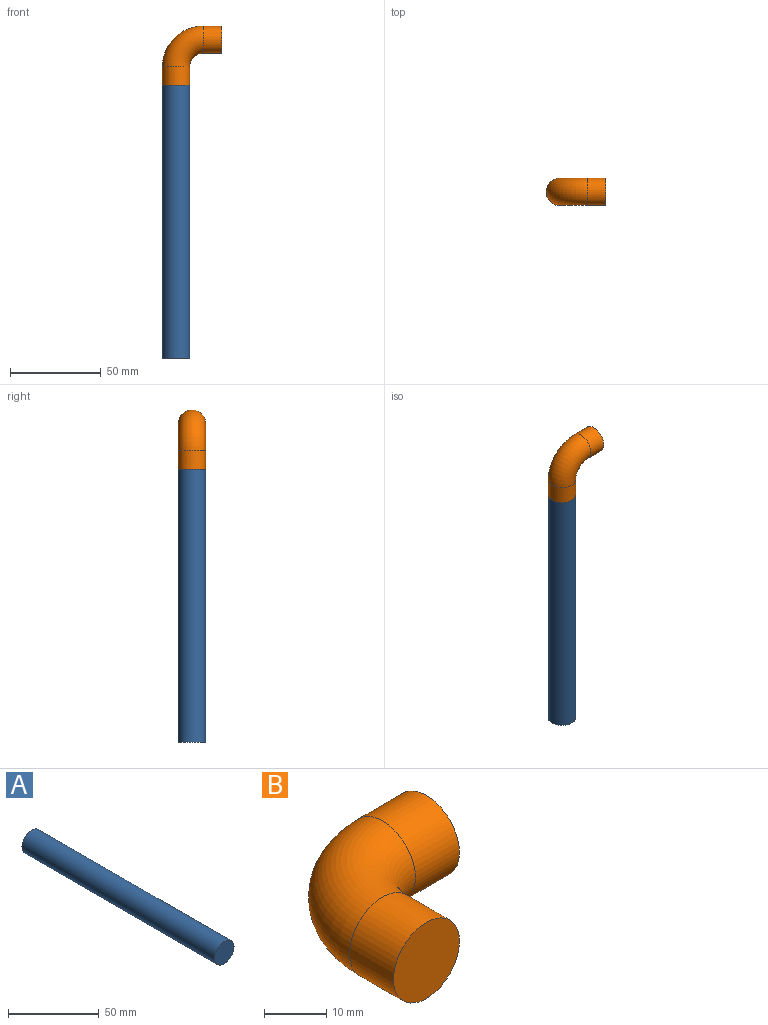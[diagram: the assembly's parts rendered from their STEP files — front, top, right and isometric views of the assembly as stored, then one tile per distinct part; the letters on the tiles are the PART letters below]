
ASSEMBLY  parts=2 mates=1
PART A: 3 faces, bbox 15x150x15 mm
  f0: cylinder r=7.5mm len=150mm, axis (0,1,0), area 7068.6mm2, adj f1,f2
  f1: plane 15x15mm, normal (0,-1,0), area 176.7mm2, adj f0
  f2: plane 15x15mm, normal (0,1,0), area 176.7mm2, adj f0
PART B: 5 faces, bbox 34.4x34.4x15 mm
  f0: plane 15x15mm, normal (0,-1,0), area 176.7mm2, adj f2
  f1: plane 15x15mm, normal (1,0,0), area 176.7mm2, adj f4
  f2: cylinder r=7.5mm len=15mm, axis (0,1,0), area 471.2mm2, adj f0,f3
  f3: torus R=15mm, axis (0,0,-1), area 1110.3mm2, adj f2,f4
  f4: cylinder r=7.5mm len=15mm, axis (1,0,0), area 471.2mm2, adj f1,f3
PLACE A rot(axis=(1,0,0),90deg) t=(1111.43,6596.59,-1350)mm
PLACE B rot(axis=(1,0,0),90deg) t=(1050,6560,-1350)mm
MATE fastened B.f2 <-> A.f0  axis (0,0,-1) through (1050,6560,-1350)mm
